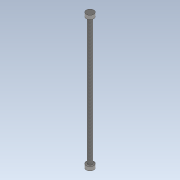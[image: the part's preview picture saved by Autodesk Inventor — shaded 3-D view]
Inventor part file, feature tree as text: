
AUTODESK INVENTOR PART (.ipt)
format: ipt  version: 2022 (Build 260153000, 153)  size: 111,616 bytes
history: native  units: mm
features: extrude x3, sketch x3, thread x1
ambient origin geometry x8: Origin, YZ Plane, XZ Plane, XY Plane, X Axis, Y Axis, Z Axis, Center Point
bodies: Solid1 (feature_tree)
feature tree (7):
  extrude  "Extrusion1"  Depth=14.0mm
  extrude  "Extrusion2"  Depth=250.0mm
  extrude  "Extrusion3"  Depth=7.0mm TaperAngle=0.0deg
  thread  "Thread1"  [1 undecoded]
  sketch  "Sketch1"  dims[d0=7.9mm d1=14.0mm]
  sketch  "Sketch2"  dims[d2=250.0mm d3=0.0mm d4=14.0mm]
  sketch  "Sketch3"  dims[d5=7.0mm d6=0.0mm d7=7.0mm d8=0.0mm d9=236.0mm d10=0.0mm]
note: 1 required parameter value undecoded (feature->parameter linkage not recoverable at this tier; creation-order binding heuristic only, values carry confidence <= 0.55)
